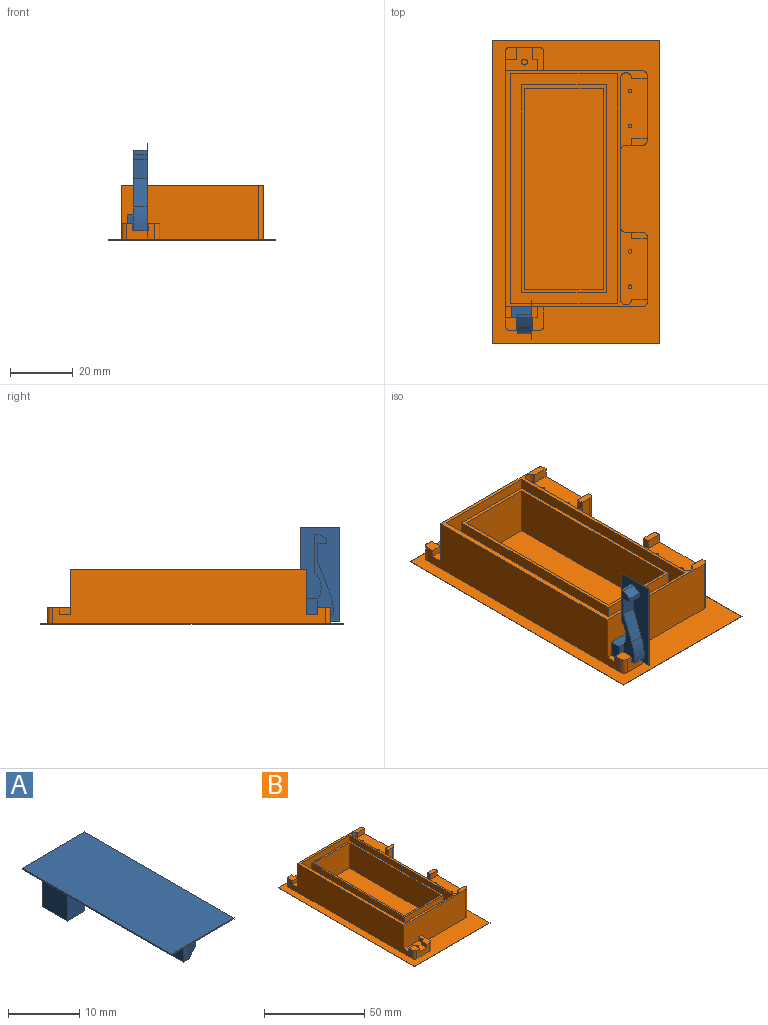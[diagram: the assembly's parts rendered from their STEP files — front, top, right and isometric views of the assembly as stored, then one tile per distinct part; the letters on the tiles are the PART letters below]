
ASSEMBLY  parts=2 mates=1
PART A: 24 faces, bbox 12.5x29.6x6.6 mm
  f0: plane 6.4x3.5mm, normal (0,-1,0), area 22.4mm2, adj f1,f11,f13,f14,f21
  f1: cylinder r=6.83mm len=8.48mm, axis (0,0,-1), area 40.6mm2, adj f0,f2,f12,f21
  f2: plane 12.12x4.4mm, normal (-1,0,0), area 53.3mm2, adj f1,f3,f12,f21
  f3: plane 4.4x1mm, normal (0,-1,0), area 4.4mm2, adj f2,f4,f12,f21
  f4: plane 4.4x2.8mm, normal (0.47,-0.88,0), area 14mm2, adj f3,f5,f12,f21
  f5: plane 4.4x1.5mm, normal (1,0,0), area 6.6mm2, adj f4,f6,f12,f21
  f6: plane 4.4x2.8mm, normal (0,1,0), area 12.3mm2, adj f5,f7,f12,f21
  f7: plane 6x4.4mm, normal (1,0,0), area 26.4mm2, adj f6,f8,f12,f21
  f8: plane 9.05x4.4mm, normal (0.93,-0.37,0), area 42.8mm2, adj f7,f12,f21,f23
  f9: plane 4.4x0.18mm, normal (1,0,0), area 0.8mm2, adj f10,f12,f21,f23
  f10: plane 8.5x6.4mm, normal (0,1,0), area 41.3mm2, adj f9,f11,f12,f13,f14,f15,f21
  f11: plane 6.4x5mm, normal (-1,0,0), area 32mm2, adj f0,f10,f14,f21
  f12: plane 25.6x6mm, normal (0,0,-1), area 64.5mm2, adj f1,f2,f3,f4,f5,f6,f7,f8
  f13: plane 5x2mm, normal (1,0,0), area 10mm2, adj f0,f10,f12,f14
  f14: plane 5x3.5mm, normal (0,0,-1), area 17.5mm2, adj f0,f10,f11,f13
  f15: cylinder r=1mm len=4.5mm, axis (0,1,0), area 28.3mm2, adj f10,f16
  f16: plane 2x2mm, normal (0,1,0), area 3.1mm2, adj f15
  f17: plane 29.6x0.2mm, normal (-1,0,0), area 5.9mm2, adj f18,f20,f21,f22
  f18: plane 12.5x0.2mm, normal (0,-1,0), area 2.5mm2, adj f17,f19,f21,f22
  f19: plane 29.6x0.2mm, normal (1,0,0), area 5.9mm2, adj f18,f20,f21,f22
  f20: plane 12.5x0.2mm, normal (0,1,0), area 2.5mm2, adj f17,f19,f21,f22
  f21: plane 29.6x12.5mm, normal (0,0,-1), area 288mm2, adj f0,f1,f2,f3,f4,f5,f6,f7
  f22: plane 29.6x12.5mm, normal (0,0,1), area 370mm2, adj f17,f18,f19,f20
  f23: cylinder r=20mm len=7.38mm, axis (0,0,-1), area 33.2mm2, adj f8,f9,f12,f21
PART B: 84 faces, bbox 53.2x96x17.5 mm
  f0: plane 4x3.55mm, normal (0,0,1), area 13.7mm2, adj f1,f20,f55,f65,f83
  f1: plane 86.83x17.4mm, normal (-1,0,0), area 1349.9mm2, adj f0,f2,f3,f4,f5,f19,f55,f57
  f2: plane 10.34x7.5mm, normal (0,0,1), area 54.4mm2, adj f1,f3,f9,f20,f65,f66,f67,f81
  f3: plane 43.55x17.4mm, normal (0,-1,0), area 717.9mm2, adj f1,f2,f19,f21,f22,f59,f68,f81
  f4: plane 43.55x17.4mm, normal (0,1,0), area 717.9mm2, adj f1,f6,f8,f19,f60,f61,f68,f80
  f5: plane 4x3.55mm, normal (0,0,1), area 13.7mm2, adj f1,f7,f57,f63,f82
  f6: plane 7.5x3.55mm, normal (0,0,1), area 20.5mm2, adj f4,f7,f8,f58,f62,f64,f80
  f7: plane 9.13x5.1mm, normal (0,1,0), area 35.1mm2, adj f5,f6,f57,f58,f61,f62,f63,f68
  f8: plane 5.91x5.1mm, normal (1,0,0), area 30.2mm2, adj f4,f6,f58,f68
  f9: cylinder r=0.9mm len=2.9mm, axis (0,0,1), area 16.4mm2, adj f2,f78
  f10: cylinder r=0.9mm len=2.9mm, axis (0,0,1), area 16.4mm2, adj f61,f77
  f11: plane 17.4x5.33mm, normal (0,1,0), area 86.9mm2, adj f14,f42,f45,f53,f54,f68
  f12: plane 5x3mm, normal (0,1,0), area 15mm2, adj f15,f17,f40,f46
  f13: plane 5x3mm, normal (0,-1,0), area 15mm2, adj f14,f16,f42,f45
  f14: plane 5x2.11mm, normal (0,0,1), area 10mm2, adj f11,f13,f16,f45,f54
  f15: plane 5x2.11mm, normal (0,0,1), area 10mm2, adj f12,f17,f23,f46,f51
  f16: plane 20.52x17.4mm, normal (1,0,0), area 299.5mm2, adj f13,f14,f19,f41,f42,f54,f59,f68
  f17: plane 20.52x17.4mm, normal (1,0,0), area 299.5mm2, adj f12,f15,f19,f39,f40,f51,f60,f68
  f18: plane 66x27mm, normal (0,0,1), area 182mm2, adj f25,f26,f27,f32,f34,f35,f36,f37
  f19: plane 75x45.14mm, normal (0,0,1), area 296mm2, adj f1,f3,f4,f16,f17,f24,f28,f29
  f20: plane 9.13x5.1mm, normal (0,-1,0), area 35.1mm2, adj f0,f2,f22,f55,f56,f65,f66,f68
  f21: plane 5.91x5.1mm, normal (1,0,0), area 30.2mm2, adj f3,f22,f56,f68
  f22: plane 7.5x3.55mm, normal (0,0,1), area 20.5mm2, adj f3,f20,f21,f56,f66,f67,f81
  f23: plane 17.4x5.33mm, normal (0,-1,0), area 86.9mm2, adj f15,f40,f46,f51,f52,f68
  f24: plane 70.23x17.4mm, normal (1,0,0), area 562.5mm2, adj f19,f40,f42,f43,f44,f52,f53,f68
  f25: plane 27x6.4mm, normal (0,-1,0), area 172.8mm2, adj f18,f26,f32,f33
  f26: plane 66x6.4mm, normal (-1,0,0), area 422.4mm2, adj f18,f25,f27,f33
  f27: plane 27x6.4mm, normal (0,1,0), area 172.8mm2, adj f18,f26,f32,f33
  f28: plane 73x6.4mm, normal (1,0,0), area 467.2mm2, adj f19,f29,f31,f33
  f29: plane 34x6.4mm, normal (0,1,0), area 217.6mm2, adj f19,f28,f30,f33
  f30: plane 73x6.4mm, normal (-1,0,0), area 467.2mm2, adj f19,f29,f31,f33
  f31: plane 34x6.4mm, normal (0,-1,0), area 217.6mm2, adj f19,f28,f30,f33
  f32: plane 66x6.4mm, normal (1,0,0), area 422.4mm2, adj f18,f25,f27,f33
  f33: plane 73x34mm, normal (0,0,1), area 700mm2, adj f25,f26,f27,f28,f29,f30,f31,f32
  f34: plane 25x15.5mm, normal (0,-1,0), area 387.5mm2, adj f18,f35,f37,f38
  f35: plane 64x15.5mm, normal (1,0,0), area 992mm2, adj f18,f34,f36,f38
  f36: plane 25x15.5mm, normal (0,1,0), area 387.5mm2, adj f18,f35,f37,f38
  f37: plane 64x15.5mm, normal (-1,0,0), area 992mm2, adj f18,f34,f36,f38
  f38: plane 64x25mm, normal (0,0,1), area 1600mm2, adj f34,f35,f36,f37
  f39: plane 5x3mm, normal (0,-1,0), area 15mm2, adj f17,f19,f40,f44
  f40: plane 24.65x8.5mm, normal (0,0,1), area 173.9mm2, adj f12,f17,f23,f24,f39,f44,f46,f48
  f41: plane 5x3mm, normal (0,1,0), area 15mm2, adj f16,f19,f42,f43
  f42: plane 24.65x8.5mm, normal (0,0,1), area 173.9mm2, adj f11,f13,f16,f24,f41,f43,f45,f47
  f43: cylinder r=1.75mm len=3.5mm, axis (0,0,1), area 16.5mm2, adj f19,f24,f41,f42
  f44: cylinder r=1.75mm len=3.5mm, axis (0,0,1), area 16.5mm2, adj f19,f24,f39,f40
  f45: plane 3x2.11mm, normal (-1,0,0), area 6.3mm2, adj f11,f13,f14,f42
  f46: plane 3x2.11mm, normal (-1,0,0), area 6.3mm2, adj f12,f15,f23,f40
  f47: cylinder r=0.57mm len=14.4mm, axis (0,0,1), area 51.7mm2, adj f42,f76
  f48: cylinder r=0.57mm len=14.4mm, axis (0,0,1), area 51.7mm2, adj f40,f75
  f49: cylinder r=0.57mm len=14.4mm, axis (0,0,1), area 51.7mm2, adj f40,f74
  f50: cylinder r=0.57mm len=14.4mm, axis (0,0,1), area 51.7mm2, adj f42,f73
  f51: cylinder r=1.59mm len=17.4mm, axis (0,0,-1), area 43.4mm2, adj f15,f17,f23,f68
  f52: cylinder r=1.59mm len=14.4mm, axis (0,0,-1), area 35.9mm2, adj f23,f24,f40,f68
  f53: cylinder r=1.59mm len=14.4mm, axis (0,0,1), area 35.9mm2, adj f11,f24,f42,f68
  f54: cylinder r=1.59mm len=17.4mm, axis (0,0,1), area 43.4mm2, adj f11,f14,f16,f68
  f55: cylinder r=1.59mm len=5.1mm, axis (0,0,1), area 12.7mm2, adj f0,f1,f20,f68
  f56: cylinder r=1.59mm len=5.1mm, axis (0,0,-1), area 12.7mm2, adj f20,f21,f22,f68
  f57: cylinder r=1.59mm len=5.1mm, axis (0,0,1), area 12.7mm2, adj f1,f5,f7,f68
  f58: cylinder r=1.59mm len=5.1mm, axis (0,0,-1), area 12.7mm2, adj f6,f7,f8,f68
  f59: cylinder r=1.59mm len=17.4mm, axis (0,0,1), area 43.4mm2, adj f3,f16,f19,f68
  f60: cylinder r=1.59mm len=17.4mm, axis (0,0,-1), area 43.4mm2, adj f4,f17,f19,f68
  f61: plane 10.34x7.5mm, normal (0,0,1), area 54.4mm2, adj f1,f4,f7,f10,f62,f63,f64,f80
  f62: plane 4x2.2mm, normal (-1,0,0), area 8.8mm2, adj f6,f7,f61,f64
  f63: plane 4x2.2mm, normal (1,0,0), area 8.8mm2, adj f5,f7,f61,f82
  f64: plane 2.2x1.59mm, normal (0,-1,0), area 3.5mm2, adj f6,f61,f62,f80
  f65: plane 4x2.2mm, normal (1,0,0), area 8.8mm2, adj f0,f2,f20,f83
  f66: plane 4x2.2mm, normal (-1,0,0), area 8.8mm2, adj f2,f20,f22,f67
  f67: plane 2.2x1.59mm, normal (0,1,0), area 3.5mm2, adj f2,f22,f66,f81
  f68: plane 96x53.2mm, normal (0,0,1), area 1775mm2, adj f1,f3,f4,f7,f8,f11,f16,f17
  f69: plane 96x0.1mm, normal (1,0,0), area 9.6mm2, adj f68,f70,f72,f79
  f70: plane 53.2x0.1mm, normal (0,-1,0), area 5.3mm2, adj f68,f69,f71,f79
  f71: plane 96x0.1mm, normal (-1,0,0), area 9.6mm2, adj f68,f70,f72,f79
  f72: plane 53.2x0.1mm, normal (0,1,0), area 5.3mm2, adj f68,f69,f71,f79
  f73: plane 1.14x1.14mm, normal (0,0,1), area 1mm2, adj f50
  f74: plane 1.14x1.14mm, normal (0,0,1), area 1mm2, adj f49
  f75: plane 1.14x1.14mm, normal (0,0,1), area 1mm2, adj f48
  f76: plane 1.14x1.14mm, normal (0,0,1), area 1mm2, adj f47
  f77: plane 1.8x1.8mm, normal (0,0,1), area 2.5mm2, adj f10
  f78: plane 1.8x1.8mm, normal (0,0,1), area 2.5mm2, adj f9
  f79: plane 96x53.2mm, normal (0,0,-1), area 5107.2mm2, adj f69,f70,f71,f72
  f80: plane 3.5x2.2mm, normal (-1,0,0), area 7.7mm2, adj f4,f6,f61,f64
  f81: plane 3.5x2.2mm, normal (-1,0,0), area 7.7mm2, adj f2,f3,f22,f67
  f82: plane 3.55x2.2mm, normal (0,-1,0), area 7.8mm2, adj f1,f5,f61,f63
  f83: plane 3.55x2.2mm, normal (0,1,0), area 7.8mm2, adj f0,f1,f2,f65
PLACE A rot(axis=(-0.58,0.58,-0.58),120deg) t=(-23.13,-39.64,31.09)mm
PLACE B t=(18.16,-37.14,23.09)mm
MATE fastened A.f15 <-> B.f9  axis (0,0,-1) through (-20.83,-39.89,26.09)mm
